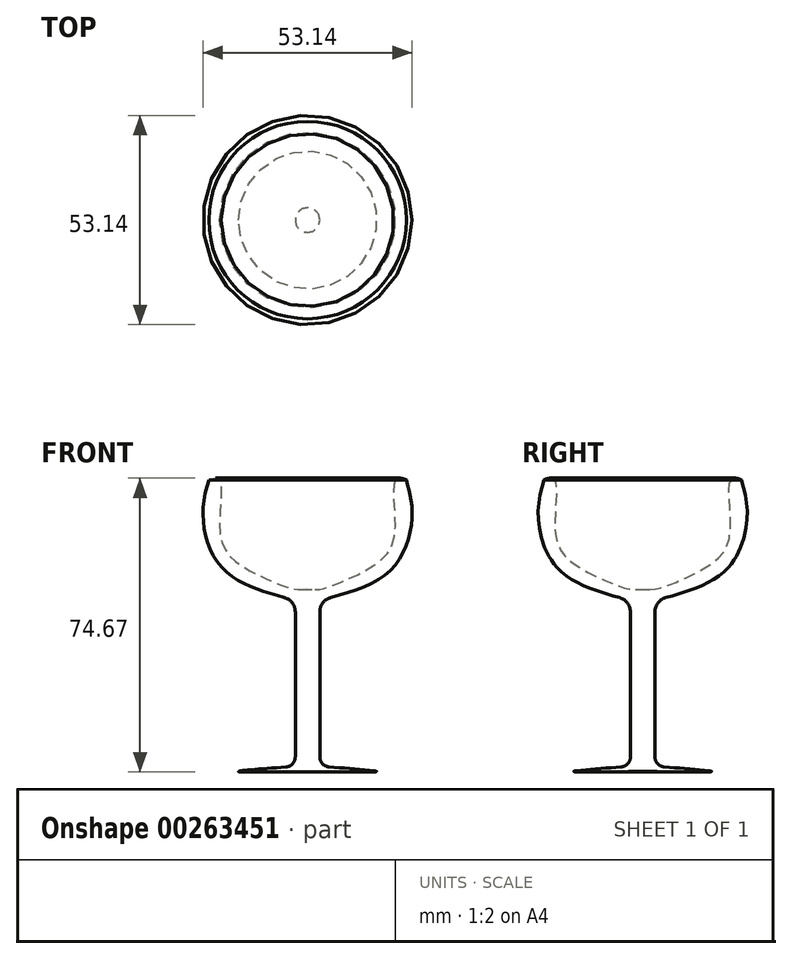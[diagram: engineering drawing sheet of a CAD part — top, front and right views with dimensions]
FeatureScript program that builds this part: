
annotation { "Feature Type Name" : "Feature", "Feature Type Description" : "" }
export const myFeature = defineFeature(function(context is Context, id is Id, definition is map)
    precondition{}
    {
        {
            var Q0;
            Q0=qCreatedBy(makeId("Front.planeOp"),FACE);
            var sketch = newSketch(context, id + "F0", { "sketchPlane" : qUnion([Q0])});
            skFitSpline(sketch, "E0", {"points": [v(0, 0) * mm, v(-17.54, 0) * mm, v(-3.12, 1.32) * mm], "startDerivative": vector(-50.2, -0.73) * mm, "endDerivative": vector(45.49, 3.43) * mm});
            skLineSegment(sketch, "E1", {"start": v(-3.12, 3.67) * mm, "end": v(-3.12, 40.51) * mm});
            skFitSpline(sketch, "E2", {"points": [v(-3.12, 43.45) * mm, v(-21.48, 51.49) * mm, v(-26.56, 65.1) * mm, v(-25.09, 74.11) * mm], "startDerivative": vector(-53.77, 13.97) * mm, "endDerivative": vector(8.69, 31.08) * mm});
            skArc(sketch, "E3.filletArc", {"start": v(-3.12, 40.51) * mm, "mid": v(-3.9, 42.83) * mm, "end": v(-5.94, 44.2) * mm});
            skArc(sketch, "E4.filletArc", {"start": v(-5.46, 1.14) * mm, "mid": v(-3.8, 1.95) * mm, "end": v(-3.12, 3.67) * mm});
            skPoint(sketch, "E5.start.orphan", {"position": v(0, 74.11) * mm});
            skFitSpline(sketch, "E6", {"points": [v(-25.09, 74.11) * mm, v(-22.43, 74.11) * mm, v(-22.27, 61.35) * mm, v(-18.4, 53.46) * mm, v(-9.43, 48.5) * mm, v(-3.4, 46.34) * mm, v(0, 46.34) * mm], "startDerivative": vector(30.68, 10.3) * mm, "endDerivative": vector(27.68, 2.6) * mm});
            skLineSegment(sketch, "E7", {"start": v(0, 46.34) * mm, "end": v(0, 0) * mm});
            skSolve(sketch);
        }
        {
            var Q0;
            Q0=makeQuery(id+"F0.imprint","IMPRINT",FACE,{"disambiguationData":[TD([[makeQuery(id+"F0.imprint","IMPRINT",EDGE,{"derivedFrom":sQuery(id+"F0.wireOp",EDGE,"E0")}),-1.0]])]});
            var Q1;
            Q1=sQuery(id+"F0.wireOp",EDGE,"E7");
            revolve(context, id + "F1", {"entities" : qUnion([Q0]), "axis" : qUnion([Q1]), "revolveType" : RevolveType.FULL});
        }
    });
